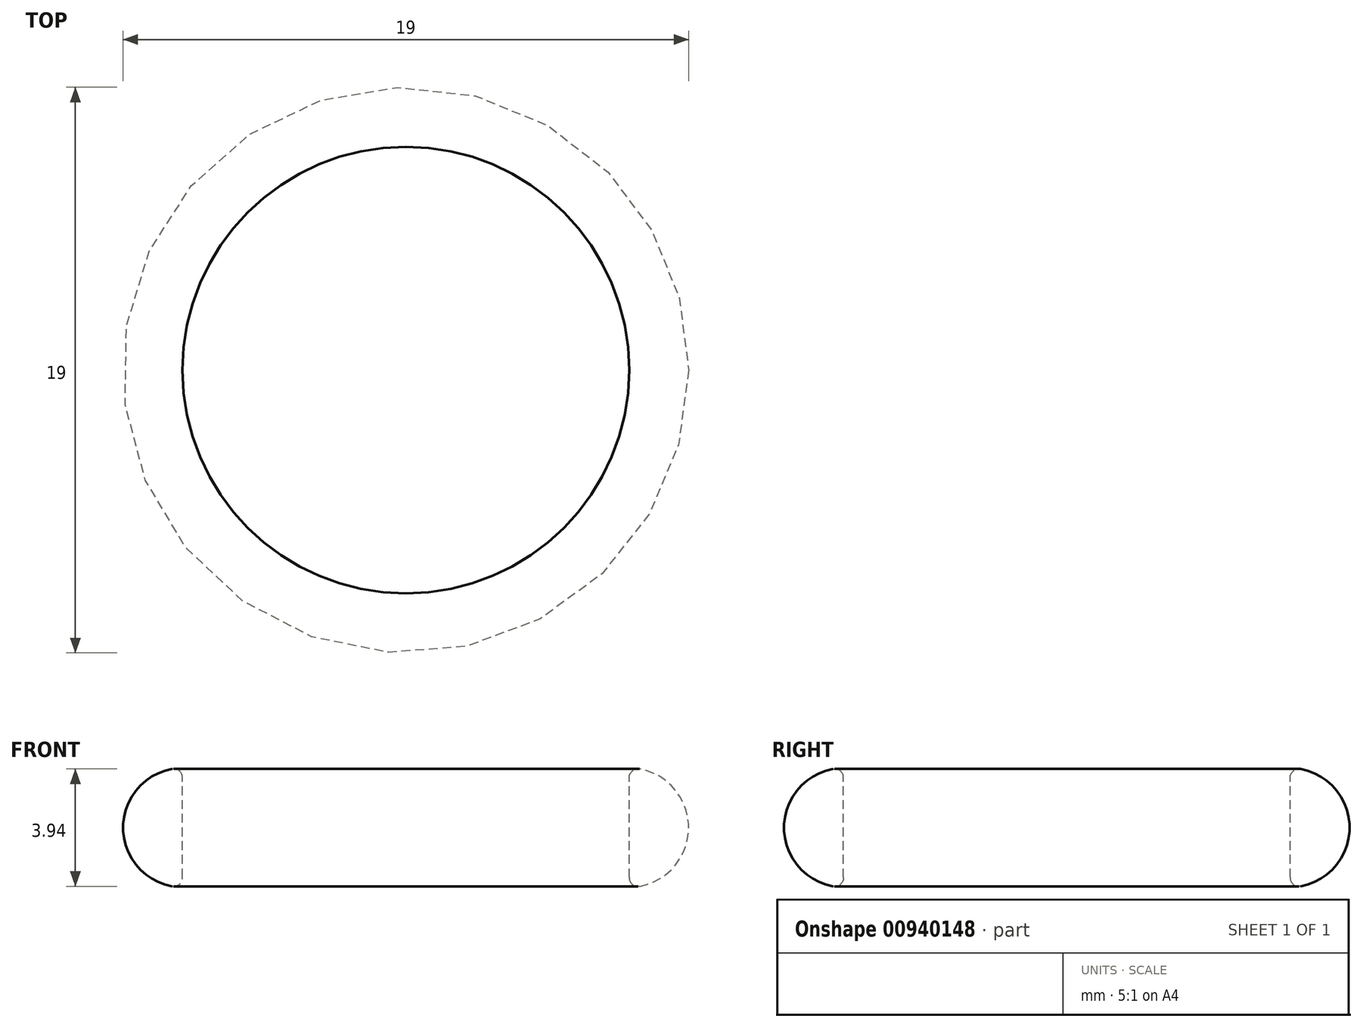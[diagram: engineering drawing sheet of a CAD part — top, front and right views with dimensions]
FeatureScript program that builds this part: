
annotation { "Feature Type Name" : "Feature", "Feature Type Description" : "" }
export const myFeature = defineFeature(function(context is Context, id is Id, definition is map)
    precondition{}
    {
        {
            var Q0;
            Q0=qCreatedBy(makeId("Top.planeOp"),FACE);
            var sketch = newSketch(context, id + "F0", { "sketchPlane" : qUnion([Q0])});
            skCircle(sketch, "E0", {"center": v(0, 0) * mm, "radius": 7.5 * mm});
            skLineSegment(sketch, "E1", {"start": v(0, 0) * mm, "end": v(7.5, 0) * mm});
            skSolve(sketch);
        }
        {
            var Q0;
            Q0=qCreatedBy(makeId("Front.planeOp"),FACE);
            var sketch = newSketch(context, id + "F1", { "sketchPlane" : qUnion([Q0])});
            skLineSegment(sketch, "E2", {"start": v(7.5, 0) * mm, "end": v(7.5, 4) * mm});
            skArc(sketch, "E3", {"start": v(7.5, 0) * mm, "mid": v(9.5, 2) * mm, "end": v(7.5, 4) * mm});
            skSolve(sketch);
        }
        {
            var Q0;
            Q0=makeQuery(id+"F1.imprint","IMPRINT",FACE,{"disambiguationData":[TD([[makeQuery(id+"F1.imprint","IMPRINT",EDGE,{"derivedFrom":sQuery(id+"F1.wireOp",EDGE,"E2")}),-1.0]])]});
            var Q1;
            Q1=sQuery(id+"F0.wireOp",EDGE,"E0");
            sweep(context, id + "F2", {"profiles" : qUnion([Q0]), "path" : qUnion([Q1])});
        }
        {
            var Q0;
            {var subQ0=sQuery(id+"F1.wireOp",EDGE,"E3");var subQ1=sQuery(id+"F1.wireOp",EDGE,"E2");var subQ2=sQuery(id+"F0.wireOp",EDGE,"E0");Q0=makeQuery(id+"F2.opSweep","SWEPT_EDGE",EDGE,{"disambiguationData":[OSD([subQ2,subQ1,subQ0]),TDD([subQ2,makeQuery(id+"F1.imprint","INTERSECT",VERTEX,{"disambiguationData":[OD(1.0)],"derivedFrom":[subQ1,subQ0]})])]});}
            var Q1;
            {var subQ0=sQuery(id+"F1.wireOp",EDGE,"E3");var subQ1=sQuery(id+"F1.wireOp",EDGE,"E2");var subQ2=sQuery(id+"F0.wireOp",EDGE,"E0");Q1=makeQuery(id+"F2.opSweep","SWEPT_EDGE",EDGE,{"disambiguationData":[OSD([subQ2,subQ1,subQ0]),TDD([subQ2,makeQuery(id+"F1.imprint","INTERSECT",VERTEX,{"disambiguationData":[OD(0.0)],"derivedFrom":[subQ1,subQ0]})])]});}
            fillet(context, id + "F3", {"entities" : qUnion([Q0, Q1]), "radius" : 0.3 * mm, "tangentPropagation" : true, "allowEdgeOverflow" : false});
        }
    });
